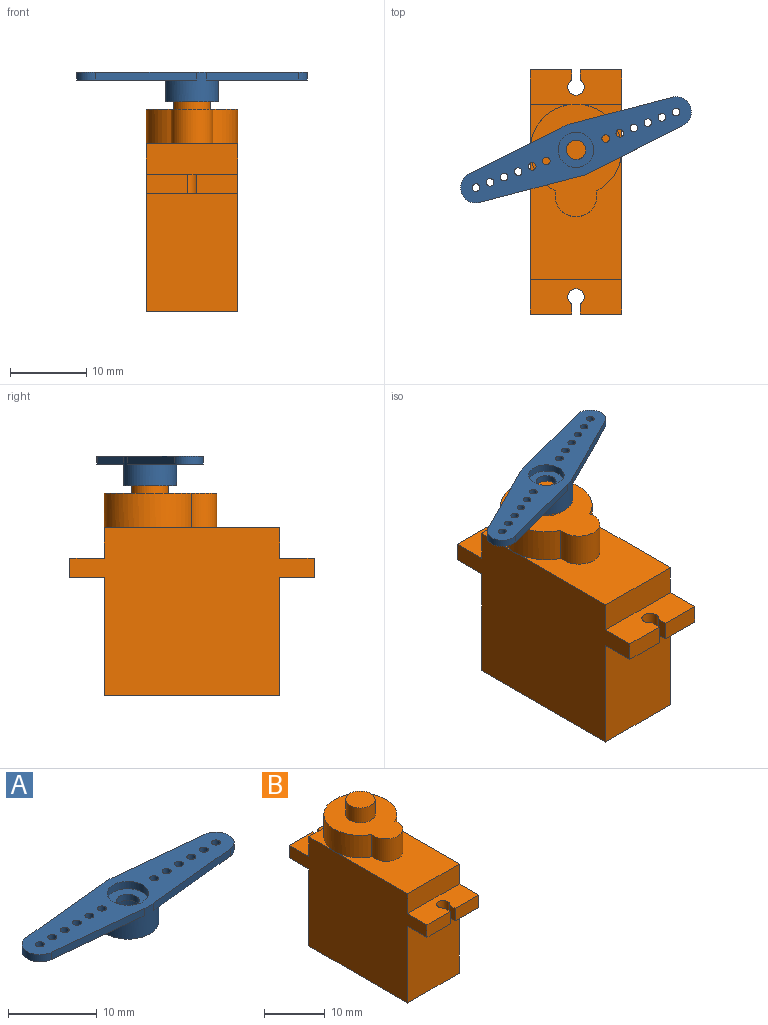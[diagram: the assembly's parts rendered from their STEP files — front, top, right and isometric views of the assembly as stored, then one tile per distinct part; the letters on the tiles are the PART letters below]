
ASSEMBLY  parts=2 mates=1
PART A: 28 faces, bbox 32x7x3.9 mm
  f0: cylinder r=3.47mm len=6.95mm, axis (0,0,-1), area 65.1mm2, adj f1,f2,f5,f6,f8,f18,f19,f21
  f1: plane 32.05x6.95mm, normal (0,0,1), area 140.4mm2, adj f0,f5,f6,f7,f9,f12,f13,f14
  f2: plane 6.95x6.95mm, normal (0,0,-1), area 19.5mm2, adj f0,f3
  f3: cylinder r=2.43mm len=4.85mm, axis (0,0,-1), area 30.5mm2, adj f2,f4
  f4: plane 4.85x4.85mm, normal (0,0,-1), area 13.4mm2, adj f3,f11
  f5: plane 13.51x1.4mm, normal (0.1,0.99,0), area 13.6mm2, adj f0,f1,f7,f8
  f6: plane 13.51x1.4mm, normal (0.1,-0.99,0), area 13.6mm2, adj f0,f1,f7,f8
  f7: cylinder r=2.01mm len=4mm, axis (0,0,1), area 5.9mm2, adj f1,f5,f6,f8
  f8: plane 15.31x6.8mm, normal (0,0,-1), area 59.7mm2, adj f0,f5,f6,f7,f12,f13,f14,f15
  f9: cylinder r=2.32mm len=4.65mm, axis (0,0,1), area 14.6mm2, adj f1,f10
  f10: plane 4.65x4.65mm, normal (0,0,1), area 11.9mm2, adj f9,f11
  f11: cylinder r=1.28mm len=2.55mm, axis (0,0,1), area 6.8mm2, adj f4,f10
  f12: cylinder r=0.5mm len=1mm, axis (0,0,1), area 3.1mm2, adj f1,f8
  f13: cylinder r=0.5mm len=1mm, axis (0,0,1), area 3.1mm2, adj f1,f8
  f14: cylinder r=0.5mm len=1mm, axis (0,0,1), area 3.1mm2, adj f1,f8
  f15: cylinder r=0.5mm len=1mm, axis (0,0,1), area 3.1mm2, adj f1,f8
  f16: cylinder r=0.5mm len=1mm, axis (0,0,1), area 3.1mm2, adj f1,f8
  f17: cylinder r=0.5mm len=1mm, axis (0,0,1), area 3.1mm2, adj f1,f8
  f18: plane 13.51x1.4mm, normal (-0.1,0.99,0), area 13.6mm2, adj f0,f1,f20,f21
  f19: plane 13.51x1.4mm, normal (-0.1,-0.99,0), area 13.6mm2, adj f0,f1,f20,f21
  f20: cylinder r=2.01mm len=4mm, axis (0,0,1), area 5.9mm2, adj f1,f18,f19,f21
  f21: plane 15.31x6.8mm, normal (0,0,-1), area 59.7mm2, adj f0,f18,f19,f20,f22,f23,f24,f25
  f22: cylinder r=0.5mm len=1mm, axis (0,0,1), area 3.1mm2, adj f1,f21
  f23: cylinder r=0.5mm len=1mm, axis (0,0,1), area 3.1mm2, adj f1,f21
  f24: cylinder r=0.5mm len=1mm, axis (0,0,1), area 3.1mm2, adj f1,f21
  f25: cylinder r=0.5mm len=1mm, axis (0,0,1), area 3.1mm2, adj f1,f21
  f26: cylinder r=0.5mm len=1mm, axis (0,0,1), area 3.1mm2, adj f1,f21
  f27: cylinder r=0.5mm len=1mm, axis (0,0,1), area 3.1mm2, adj f1,f21
PART B: 29 faces, bbox 12x32x29.5 mm
  f0: plane 17x12mm, normal (0,0,1), area 134.4mm2, adj f9,f10,f11,f24,f25
  f1: plane 6x6mm, normal (0,0,1), area 7.7mm2, adj f8,f11,f25
  f2: plane 5.43x2.5mm, normal (0,1,0), area 13.6mm2, adj f4,f5,f11,f22
  f3: plane 5.43x2.5mm, normal (0,-1,0), area 13.6mm2, adj f11,f16,f17,f19
  f4: plane 12x4.5mm, normal (0,0,1), area 49mm2, adj f2,f8,f9,f11,f14,f21,f22,f23
  f5: plane 12x4.5mm, normal (0,0,-1), area 49mm2, adj f2,f7,f9,f11,f14,f21,f22,f23
  f6: plane 15.5x12mm, normal (0,-1,0), area 186mm2, adj f9,f11,f13,f17
  f7: plane 15.5x12mm, normal (0,1,0), area 186mm2, adj f5,f9,f11,f13
  f8: plane 12x4mm, normal (0,1,0), area 48mm2, adj f1,f4,f9,f11,f12
  f9: plane 32x22mm, normal (-1,0,0), area 528.5mm2, adj f0,f4,f5,f6,f7,f8,f10,f12
  f10: plane 12x4mm, normal (0,-1,0), area 48mm2, adj f0,f9,f11,f16
  f11: plane 32x22mm, normal (1,0,0), area 528.5mm2, adj f0,f1,f2,f3,f4,f5,f6,f7
  f12: plane 6x6mm, normal (0,0,1), area 7.7mm2, adj f8,f9,f25
  f13: plane 23x12mm, normal (0,0,-1), area 276mm2, adj f6,f7,f9,f11
  f14: plane 5.43x2.5mm, normal (0,1,0), area 13.6mm2, adj f4,f5,f9,f23
  f15: plane 5.43x2.5mm, normal (0,-1,0), area 13.6mm2, adj f9,f16,f17,f18
  f16: plane 12x4.5mm, normal (0,0,1), area 49mm2, adj f3,f9,f10,f11,f15,f18,f19,f20
  f17: plane 12x4.5mm, normal (0,0,-1), area 49mm2, adj f3,f6,f9,f11,f15,f18,f19,f20
  f18: plane 2.5x1.34mm, normal (1,0,0), area 3.4mm2, adj f15,f16,f17,f20
  f19: plane 2.5x1.34mm, normal (-1,0,0), area 3.4mm2, adj f3,f16,f17,f20
  f20: cylinder r=1.07mm len=2.5mm, axis (0,0,1), area 13.9mm2, adj f16,f17,f18,f19
  f21: cylinder r=1.07mm len=2.5mm, axis (0,0,1), area 13.9mm2, adj f4,f5,f22,f23
  f22: plane 2.5x1.34mm, normal (-1,0,0), area 3.4mm2, adj f2,f4,f5,f21
  f23: plane 2.5x1.34mm, normal (1,0,0), area 3.4mm2, adj f4,f5,f14,f21
  f24: cylinder r=2.75mm len=5.5mm, axis (0,0,-1), area 44.6mm2, adj f0,f25,f26
  f25: cylinder r=6mm len=12mm, axis (0,0,-1), area 144.7mm2, adj f0,f1,f12,f24,f26
  f26: plane 14.75x12mm, normal (0,0,1), area 107.7mm2, adj f24,f25,f27
  f27: cylinder r=2.43mm len=4.85mm, axis (0,0,-1), area 45.7mm2, adj f26,f28
  f28: plane 4.85x4.85mm, normal (0,0,1), area 18.5mm2, adj f27
PLACE A rot(axis=(0,0,1),20.7deg) t=(0,5.5,27.5)mm
PLACE B t=(-6,-11.5,0)mm
MATE revolute A.f0 <-> B.f25  axis (0,0,-1) through (0,5.5,29.5)mm
